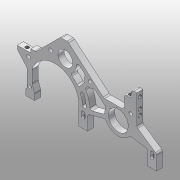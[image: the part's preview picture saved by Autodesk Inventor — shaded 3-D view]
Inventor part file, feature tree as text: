
AUTODESK INVENTOR PART (.ipt)
format: ipt  version: 2016 (Build 200138000, 138)  size: 528,384 bytes
history: native  units: mm (DEFAULTED — no unit token found)
features: sketch x12, hole x8, thread x8, extrude x5, fillet x3, imported_body x1
ambient origin geometry x8: Origin, YZ Plane, XZ Plane, XY Plane, X Axis, Y Axis, Z Axis, Center Point
bodies: Solid1 (feature_tree)
feature tree (37):
  extrude  "Extrusion1"  Depth=2.0mm
  fillet  "Fillet1"  Radius=3.0mm
  extrude  "Extrusion2"  Depth=3.0mm
  fillet  "Fillet2"  Radius=3.0mm
  hole  "Hole1"  [1 undecoded]
  thread  "Thread1"  [1 undecoded]
  hole  "Hole2"  [1 undecoded]
  thread  "Thread2"  [1 undecoded]
  extrude  "Extrusion6"  Depth=1.5mm
  hole  "Hole3"  [1 undecoded]
  thread  "Thread3"  [1 undecoded]
  hole  "Hole4"  [1 undecoded]
  thread  "Thread4"  [1 undecoded]
  hole  "Hole5"  [1 undecoded]
  thread  "Thread5"  [1 undecoded]
  hole  "Hole6"  [1 undecoded]
  thread  "Thread6"  [1 undecoded]
  hole  "Hole7"  [1 undecoded]
  thread  "Thread7"  [1 undecoded]
  hole  "Hole8"  [1 undecoded]
  thread  "Thread8"  [1 undecoded]
  extrude  "Extrusion7"  Depth=10.0mm TaperAngle=0.0deg
  fillet  "Fillet5"  Radius=10.0mm
  extrude  "Extrusion5"  Depth=2.0mm TaperAngle=0.0deg
  sketch  "Sketch3"  dims[d1=10.0mm d2=0.0mm d3=2.0mm d4=3.0mm]
  sketch  "Sketch7"  dims[d8=3.0mm d10=3.0mm d11=3.0mm]
  imported_body  "DerivedBody::500-142"
  sketch  "Sketch8"  dims[d12=3.0mm d13=3.0mm d14=3.0mm]
  sketch  "Sketch9"  dims[d15=3.0mm d17=4.5mm d20=4.5mm]
  sketch  "Sketch10"  dims[d22=10.0mm d23=0.0mm d24=1.5mm]
  sketch  "Sketch11"  dims[d31=26.5mm d32=28.0mm d33=30.0mm]
  sketch  "Sketch13"  dims[d34=2.5mm d35=4.0mm d36=4.0mm]
  sketch  "Sketch14"  dims[d37=4.5mm d38=10.0mm d39=0.0mm]
  sketch  "Sketch15"  dims[d40=3.0mm d41=6.0mm d42=4.0mm d43=2.0mm d44=90.0deg d45=7.5mm d46=20.594885mm d47=7.0mm d48=1.0mm]
  sketch  "Sketch16"  dims[d49=3.0mm d50=6.0mm d51=4.0mm d52=2.0mm d53=90.0deg d54=10.0mm d55=20.594885mm d56=10.0mm d57=0.0mm d58=10.0mm d59=0.0mm]
  sketch  "Sketch17"  dims[d60=3.0mm d61=6.0mm d62=4.0mm d63=2.0mm d64=90.0deg d65=8.0mm d66=20.594885mm d67=10.0mm d68=0.0mm]
  sketch  "Sketch18"  dims[d69=3.0mm d70=6.0mm d71=4.0mm d72=2.0mm d73=90.0deg d74=8.0mm d75=20.594885mm d76=10.0mm d77=0.0mm d78=3.0mm d79=6.0mm d80=4.0mm d81=2.0mm d82=90.0deg d83=6.0mm d84=20.594885mm d85=10.0mm d86=0.0mm d87=3.0mm d88=6.0mm d89=4.0mm d90=2.0mm d91=90.0deg d92=6.0mm d93=20.594885mm d94=10.0mm d95=0.0mm d96=3.0mm d97=6.0mm d98=4.0mm d99=2.0mm d100=90.0deg d101=6.0mm d102=20.594885mm d103=10.0mm d104=0.0mm d105=3.0mm d106=6.0mm d107=4.0mm d108=2.0mm d109=90.0deg d110=6.0mm d111=20.594885mm d112=10.0mm d113=0.0mm d115=6.25mm d116=0.0mm d117=2.0mm]
note: 16 required parameter values undecoded (feature->parameter linkage not recoverable at this tier; creation-order binding heuristic only, values carry confidence <= 0.55)
